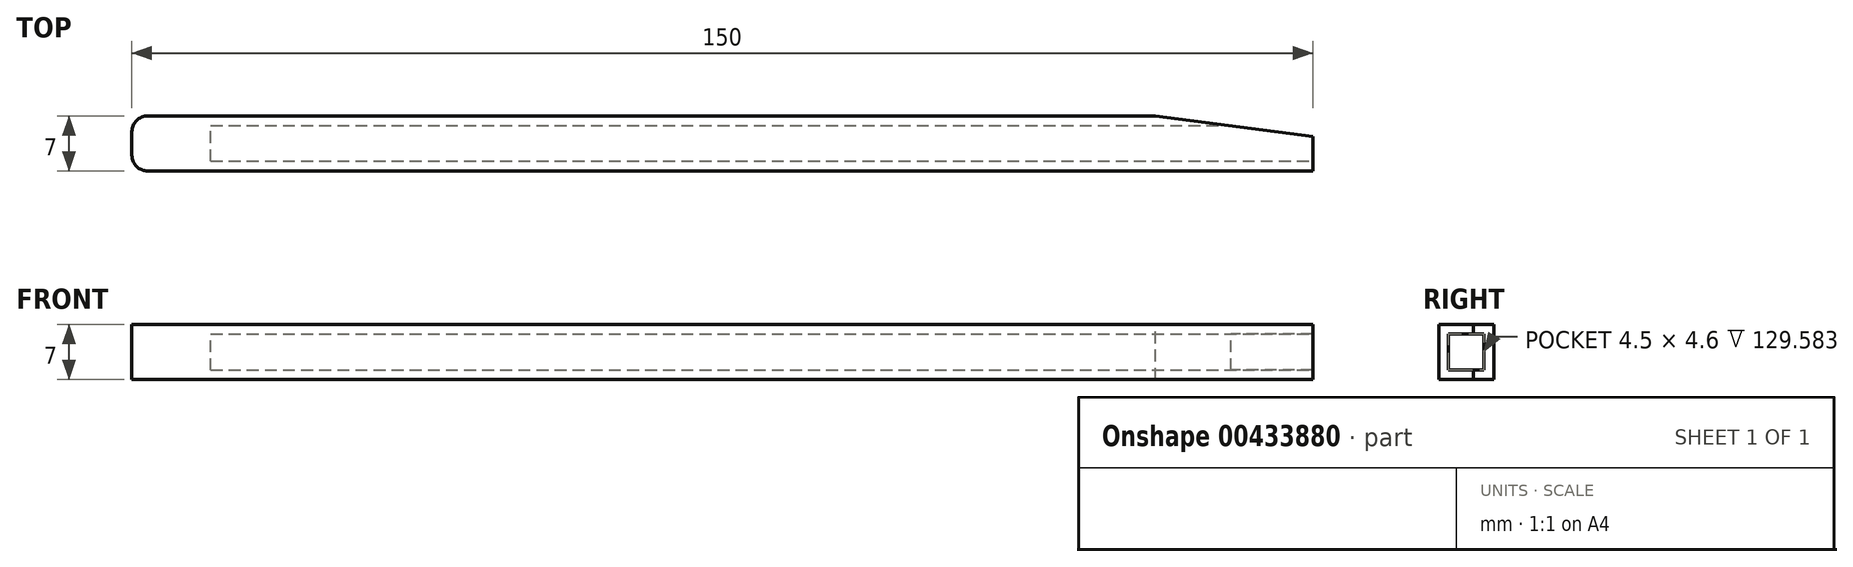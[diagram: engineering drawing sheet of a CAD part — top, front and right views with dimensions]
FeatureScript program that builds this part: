
annotation { "Feature Type Name" : "Feature", "Feature Type Description" : "" }
export const myFeature = defineFeature(function(context is Context, id is Id, definition is map)
    precondition{}
    {
        {
            var Q0;
            Q0=qCreatedBy(makeId("Front.planeOp"),FACE);
            var sketch = newSketch(context, id + "F0", { "sketchPlane" : qUnion([Q0])});
            skLineSegment(sketch, "E0.bottom", {"start": v(75, -3.5) * mm, "end": v(-75, -3.5) * mm});
            skLineSegment(sketch, "E0.top", {"start": v(75, 3.5) * mm, "end": v(-75, 3.5) * mm});
            skLineSegment(sketch, "E0.left", {"start": v(75, -3.5) * mm, "end": v(75, 3.5) * mm});
            skLineSegment(sketch, "E0.right", {"start": v(-75, -3.5) * mm, "end": v(-75, 3.5) * mm});
            skPoint(sketch, "E0.middle", {"position": v(0, 0) * mm});
            skSolve(sketch);
        }
        {
            var Q0;
            Q0=makeQuery(id+"F0.imprint","IMPRINT",FACE,{"disambiguationData":[TD([[makeQuery(id+"F0.imprint","IMPRINT",EDGE,{"derivedFrom":sQuery(id+"F0.wireOp",EDGE,"E0.bottom")}),-1.0]])]});
            extrude(context, id + "F1", {"entities" : qUnion([Q0]), "depth" : 7 * mm, "symmetric" : true});
        }
        {
            var Q0;
            Q0=makeQuery(id+"F1.opExtrude","SWEPT_FACE",FACE,{"disambiguationData":[OSD([sQuery(id+"F0.wireOp",EDGE,"E0.left")])]});
            var sketch = newSketch(context, id + "F2", { "sketchPlane" : qUnion([Q0])});
            skLineSegment(sketch, "E1.bottom", {"start": v(-2.25, -2.3) * mm, "end": v(2.25, -2.3) * mm});
            skLineSegment(sketch, "E1.top", {"start": v(-2.25, 2.3) * mm, "end": v(2.25, 2.3) * mm});
            skLineSegment(sketch, "E1.left", {"start": v(-2.25, -2.3) * mm, "end": v(-2.25, 2.3) * mm});
            skLineSegment(sketch, "E1.right", {"start": v(2.25, -2.3) * mm, "end": v(2.25, 2.3) * mm});
            skPoint(sketch, "E1.middle", {"position": v(0, 0) * mm});
            skLineSegment(sketch, "E2.bottom", {"start": v(0.9, 2.3) * mm, "end": v(-0.9, 2.3) * mm});
            skLineSegment(sketch, "E2.top", {"start": v(0.9, 3.5) * mm, "end": v(-0.9, 3.5) * mm});
            skLineSegment(sketch, "E2.left", {"start": v(0.9, 2.3) * mm, "end": v(0.9, 3.5) * mm});
            skLineSegment(sketch, "E2.right", {"start": v(-0.9, 2.3) * mm, "end": v(-0.9, 3.5) * mm});
            skPoint(sketch, "E2.middle", {"position": v(0, 2.9) * mm});
            skPoint(sketch, "E2.middle.positionSnap0", {"position": v(0, 2.3) * mm});
            skPoint(sketch, "E2.centerSnap0", {"position": v(0, 2.3) * mm});
            skSolve(sketch);
        }
        {
            var Q0;
            {var subQ0=sQuery(id+"F2.wireOp",EDGE,"E2.top");Q0=makeQuery(id+"F2.imprint","IMPRINT",FACE,{"disambiguationData":[TD([[makeQuery(id+"F2.imprint","IMPRINT",EDGE,{"derivedFrom":subQ0}),1.0]])]});}
            var Q1;
            {var subQ0=sQuery(id+"F2.wireOp",EDGE,"E2.bottom");Q1=makeQuery(id+"F2.imprint","IMPRINT",FACE,{"disambiguationData":[TD([[makeQuery(id+"F2.imprint","IMPRINT",EDGE,{"derivedFrom":subQ0}),-1.0]])]});}
            var Q2;
            Q2=makeQuery(id+"F2.imprint","IMPRINT",FACE,{"disambiguationData":[TD([[makeQuery(id+"F2.imprint","IMPRINT",EDGE,{"derivedFrom":sQuery(id+"F2.wireOp",EDGE,"E1.bottom")}),1.0]])]});
            extrude(context, id + "F3", {"entities" : qUnion([Q0, Q1, Q2]), "operationType" : NewBodyOperationType.REMOVE, "oppositeDirection" : true, "depth" : 140 * mm});
        }
        {
            var Q0;
            Q0=makeQuery(id+"F1.opExtrude","CAP_EDGE",EDGE,{"disambiguationData":[OSD([sQuery(id+"F0.wireOp",EDGE,"E0.right")])],"isStart":true});
            var Q1;
            Q1=makeQuery(id+"F1.opExtrude","CAP_EDGE",EDGE,{"disambiguationData":[OSD([sQuery(id+"F0.wireOp",EDGE,"E0.right")])],"isStart":false});
            fillet(context, id + "F4", {"entities" : qUnion([Q0, Q1]), "radius" : 2 * mm, "tangentPropagation" : true, "allowEdgeOverflow" : false});
        }
        {
            var Q0;
            Q0=makeQuery(id+"F1.opExtrude","SWEPT_FACE",FACE,{"disambiguationData":[OSD([sQuery(id+"F0.wireOp",EDGE,"E0.top")])]});
            var sketch = newSketch(context, id + "F5", { "sketchPlane" : qUnion([Q0])});
            skLineSegment(sketch, "E3", {"start": v(55, 11.48) * mm, "end": v(55, -12.11) * mm, "construction": true});
            skLineSegment(sketch, "E4", {"start": v(55, 3.5) * mm, "end": v(75, 0.9) * mm});
            skLineSegment(sketch, "E5", {"start": v(55, -3.5) * mm, "end": v(74.76, -0.9) * mm});
            skLineSegment(sketch, "E6", {"start": v(55, 3.5) * mm, "end": v(55, 3.5) * mm});
            skLineSegment(sketch, "E7", {"start": v(55, 3.5) * mm, "end": v(55, 4.89) * mm});
            skLineSegment(sketch, "E8", {"start": v(55, 4.89) * mm, "end": v(77.02, 4.89) * mm});
            skLineSegment(sketch, "E9", {"start": v(77.02, 4.89) * mm, "end": v(77.02, -5.05) * mm});
            skLineSegment(sketch, "E10", {"start": v(77.02, -5.05) * mm, "end": v(55, -5.37) * mm});
            skSolve(sketch);
        }
        {
            var Q0;
            {var subQ0=sQuery(id+"F5.wireOp",EDGE,"E4");Q0=makeQuery(id+"F5.imprint","IMPRINT",FACE,{"disambiguationData":[TD([[makeQuery(id+"F5.imprint","IMPRINT",EDGE,{"derivedFrom":subQ0}),1.0]])]});}
            var Q1;
            {var subQ0=sQuery(id+"F5.wireOp",EDGE,"E5");Q1=makeQuery(id+"F5.imprint","IMPRINT",FACE,{"disambiguationData":[TD([[makeQuery(id+"F5.imprint","IMPRINT",EDGE,{"derivedFrom":subQ0}),-1.0]])]});}
            extrude(context, id + "F6", {"entities" : qUnion([Q0, Q1]), "operationType" : NewBodyOperationType.REMOVE, "endBound" : BoundingType.THROUGH_ALL, "oppositeDirection" : true, "depth" : 25 * mm});
        }
    });
